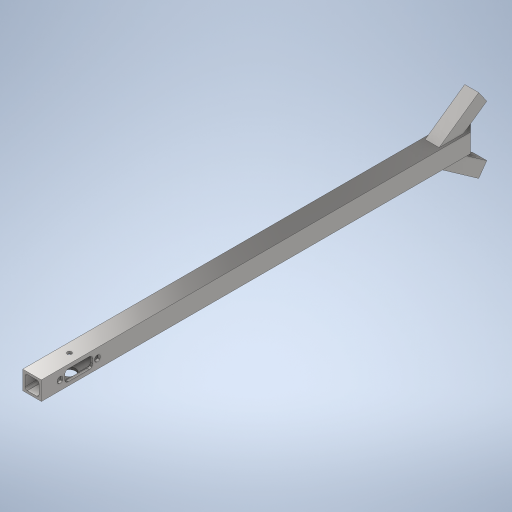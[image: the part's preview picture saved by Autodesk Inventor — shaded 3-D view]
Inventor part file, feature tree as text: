
AUTODESK INVENTOR PART (.ipt)
format: ipt  version: 2023 (Build 270158000, 158)  size: 350,720 bytes
history: native  units: in
note: dims shown in document units (in); Inventor stores cm internally (conversion verified against a paired STEP export)
features: sketch x3, extrude x2, plane x1, mirror x1, projected_geometry x1, imported_body x1
ambient origin geometry x8: Origin, YZ Plane, XZ Plane, XY Plane, X Axis, Y Axis, Z Axis, Center Point
bodies: Solid1 (feature_tree)
feature tree (9):
  sketch  "Sketch1"  dims[d0=2.561in d2=0.8134in]
  extrude  "Extrusion1"  Depth=0.8134in
  extrude  "Extrusion2"  Depth=0.875in TaperAngle=0.0deg
  plane  "Work Plane1"
  mirror  "Mirror1"
  sketch  "Sketch2"  dims[d3=1.526in d4=0.875in d5=0.0in]
  sketch  "Sketch3"  dims[d6=0.125in d7=0.0in d8=0.0in d9=0.614in]
  projected_geometry  "Projected Loop1"
  imported_body  "Base1"
